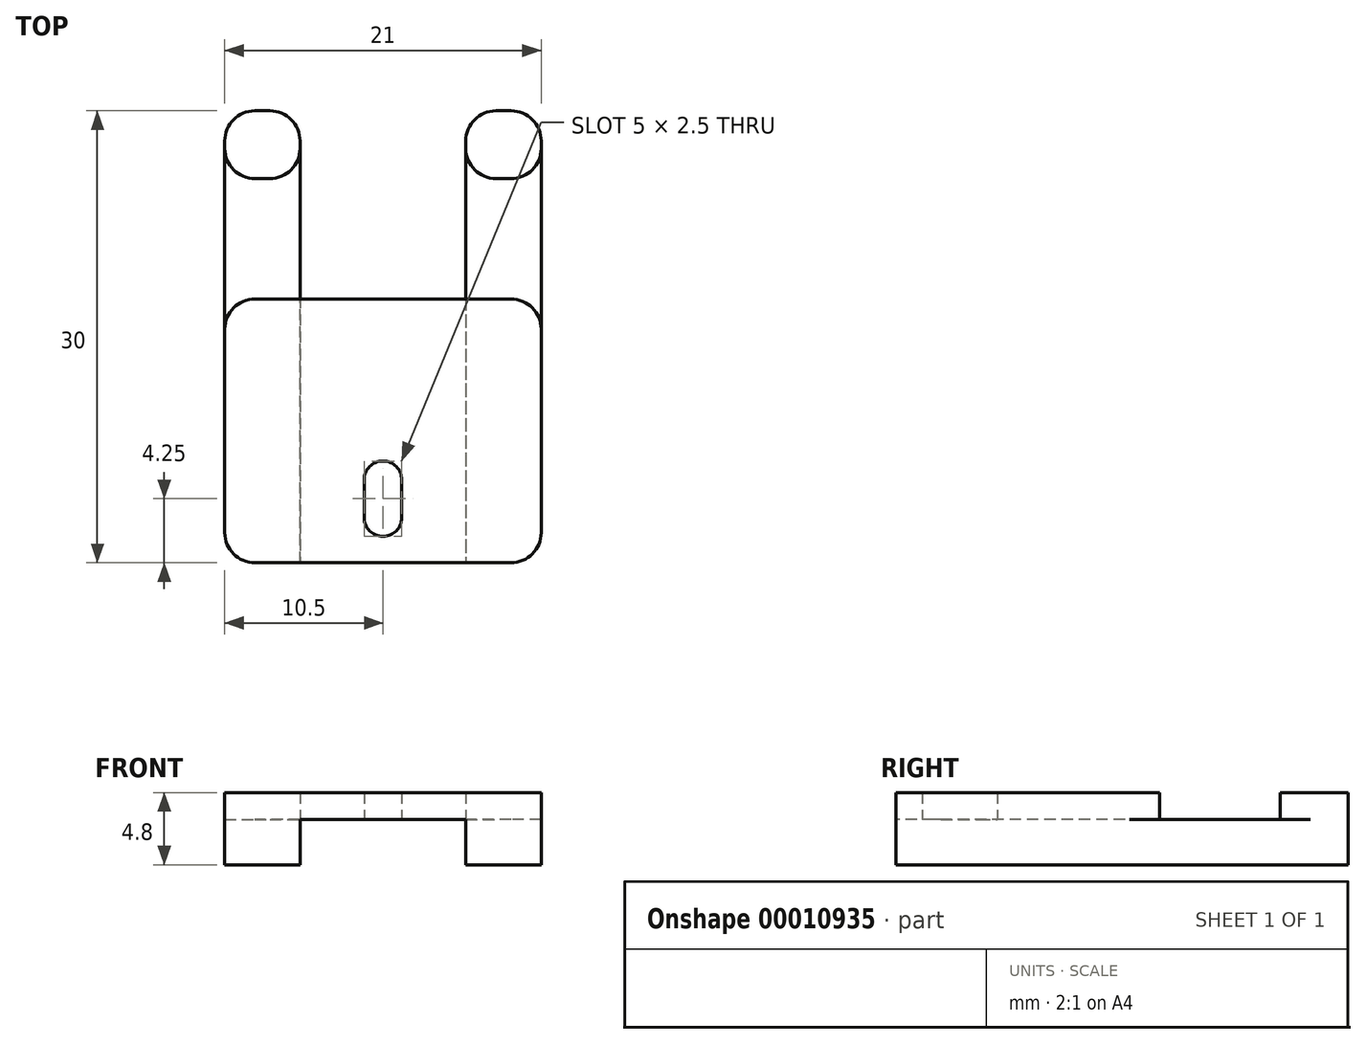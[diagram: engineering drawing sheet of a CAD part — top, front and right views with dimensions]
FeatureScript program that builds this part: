
annotation { "Feature Type Name" : "Feature", "Feature Type Description" : "" }
export const myFeature = defineFeature(function(context is Context, id is Id, definition is map)
    precondition{}
    {
        {
            var Q0;
            Q0=qCreatedBy(makeId("Top.planeOp"),FACE);
            var sketch = newSketch(context, id + "F0", { "sketchPlane" : qUnion([Q0])});
            skLineSegment(sketch, "E0", {"start": v(0, 0) * mm, "end": v(5.5, 0) * mm});
            skLineSegment(sketch, "E1.0.MirrorCS", {"start": v(0, 0) * mm, "end": v(-5.5, 0) * mm});
            skLineSegment(sketch, "E2.bottom", {"start": v(5.5, 0) * mm, "end": v(10.5, 0) * mm});
            skLineSegment(sketch, "E2.top", {"start": v(5.5, -30) * mm, "end": v(10.5, -30) * mm});
            skLineSegment(sketch, "E2.left", {"start": v(5.5, 0) * mm, "end": v(5.5, -30) * mm});
            skLineSegment(sketch, "E2.right", {"start": v(10.5, 0) * mm, "end": v(10.5, -30) * mm});
            skLineSegment(sketch, "E3.0.MirrorCS", {"start": v(-5.5, 0) * mm, "end": v(-5.5, -30) * mm});
            skLineSegment(sketch, "E4.0.MirrorCS", {"start": v(-5.5, 0) * mm, "end": v(-10.5, 0) * mm});
            skLineSegment(sketch, "E5.0.MirrorCS", {"start": v(-10.5, 0) * mm, "end": v(-10.5, -30) * mm});
            skLineSegment(sketch, "E6.0.MirrorCS", {"start": v(-5.5, -30) * mm, "end": v(-10.5, -30) * mm});
            skLineSegment(sketch, "E7", {"start": v(13, 0) * mm, "end": v(13, -4.5) * mm, "construction": true});
            skLineSegment(sketch, "E8", {"start": v(13, -4.5) * mm, "end": v(10.5, -4.5) * mm, "construction": true});
            skLineSegment(sketch, "E9", {"start": v(10.5, -4.5) * mm, "end": v(5.5, -4.5) * mm});
            skLineSegment(sketch, "E10.0.MirrorCS", {"start": v(-10.5, -4.5) * mm, "end": v(-5.5, -4.5) * mm});
            skLineSegment(sketch, "E11", {"start": v(13, -4.5) * mm, "end": v(13, -12.5) * mm, "construction": true});
            skLineSegment(sketch, "E12", {"start": v(13, -12.5) * mm, "end": v(10.5, -12.5) * mm, "construction": true});
            skLineSegment(sketch, "E13", {"start": v(10.5, -12.5) * mm, "end": v(5.5, -12.5) * mm});
            skLineSegment(sketch, "E14.0.MirrorCS", {"start": v(-10.5, -12.5) * mm, "end": v(-5.5, -12.5) * mm});
            skLineSegment(sketch, "E15", {"start": v(5.5, -12.5) * mm, "end": v(0, -12.5) * mm});
            skLineSegment(sketch, "E16", {"start": v(5.5, -30) * mm, "end": v(0, -30) * mm});
            skLineSegment(sketch, "E17.0.MirrorCS", {"start": v(-5.5, -12.5) * mm, "end": v(0, -12.5) * mm});
            skLineSegment(sketch, "E18.0.MirrorCS", {"start": v(-5.5, -30) * mm, "end": v(0, -30) * mm});
            skLineSegment(sketch, "E19", {"start": v(0, -12.5) * mm, "end": v(0, -24.5) * mm, "construction": true});
            skCircle(sketch, "E20", {"center": v(0, -24.5) * mm, "radius": 1.25 * mm});
            skLineSegment(sketch, "E21", {"start": v(-1.25, -27) * mm, "end": v(-1.25, -24.5) * mm});
            skLineSegment(sketch, "E22.0.MirrorCS", {"start": v(1.25, -27) * mm, "end": v(1.25, -24.5) * mm});
            skLineSegment(sketch, "E23", {"start": v(0, -24.5) * mm, "end": v(0, -27) * mm, "construction": true});
            skCircle(sketch, "E24", {"center": v(0, -27) * mm, "radius": 1.25 * mm});
            skSolve(sketch);
        }
        {
            var Q0;
            {var subQ2=sQuery(id+"F0.wireOp",EDGE,"E2.top");Q0=makeQuery(id+"F0.imprint","IMPRINT",FACE,{"disambiguationData":[TD([[makeQuery(id+"F0.imprint","IMPRINT",EDGE,{"derivedFrom":subQ2}),1.0]])]});}
            var Q1;
            {var subQ3=sQuery(id+"F0.wireOp",EDGE,"E15");Q1=makeQuery(id+"F0.imprint","IMPRINT",FACE,{"disambiguationData":[TD([[makeQuery(id+"F0.imprint","IMPRINT",EDGE,{"derivedFrom":subQ3}),1.0]])]});}
            var Q2;
            {var subQ1=sQuery(id+"F0.wireOp",EDGE,"E6.0.MirrorCS");Q2=makeQuery(id+"F0.imprint","IMPRINT",FACE,{"disambiguationData":[TD([[makeQuery(id+"F0.imprint","IMPRINT",EDGE,{"derivedFrom":subQ1}),-1.0]])]});}
            var Q3;
            {var subQ2=sQuery(id+"F0.wireOp",EDGE,"E2.bottom");Q3=makeQuery(id+"F0.imprint","IMPRINT",FACE,{"disambiguationData":[TD([[makeQuery(id+"F0.imprint","IMPRINT",EDGE,{"derivedFrom":subQ2}),-1.0]])]});}
            var Q4;
            {var subQ2=sQuery(id+"F0.wireOp",EDGE,"E4.0.MirrorCS");Q4=makeQuery(id+"F0.imprint","IMPRINT",FACE,{"disambiguationData":[TD([[makeQuery(id+"F0.imprint","IMPRINT",EDGE,{"derivedFrom":subQ2}),1.0]])]});}
            extrude(context, id + "F1", {"entities" : qUnion([Q0, Q1, Q2, Q3, Q4]), "depth" : 1.8 * mm});
        }
        {
            var Q0;
            {var subQ2=sQuery(id+"F0.wireOp",EDGE,"E4.0.MirrorCS");Q0=makeQuery(id+"F0.imprint","IMPRINT",FACE,{"disambiguationData":[TD([[makeQuery(id+"F0.imprint","IMPRINT",EDGE,{"derivedFrom":subQ2}),1.0]])]});}
            var Q1;
            {var subQ1=sQuery(id+"F0.wireOp",EDGE,"E10.0.MirrorCS");Q1=makeQuery(id+"F0.imprint","IMPRINT",FACE,{"disambiguationData":[TD([[makeQuery(id+"F0.imprint","IMPRINT",EDGE,{"derivedFrom":subQ1}),-1.0]])]});}
            var Q2;
            {var subQ1=sQuery(id+"F0.wireOp",EDGE,"E6.0.MirrorCS");Q2=makeQuery(id+"F0.imprint","IMPRINT",FACE,{"disambiguationData":[TD([[makeQuery(id+"F0.imprint","IMPRINT",EDGE,{"derivedFrom":subQ1}),-1.0]])]});}
            var Q3;
            {var subQ2=sQuery(id+"F0.wireOp",EDGE,"E2.top");Q3=makeQuery(id+"F0.imprint","IMPRINT",FACE,{"disambiguationData":[TD([[makeQuery(id+"F0.imprint","IMPRINT",EDGE,{"derivedFrom":subQ2}),1.0]])]});}
            var Q4;
            {var subQ1=sQuery(id+"F0.wireOp",EDGE,"E9");Q4=makeQuery(id+"F0.imprint","IMPRINT",FACE,{"disambiguationData":[TD([[makeQuery(id+"F0.imprint","IMPRINT",EDGE,{"derivedFrom":subQ1}),1.0]])]});}
            var Q5;
            {var subQ2=sQuery(id+"F0.wireOp",EDGE,"E2.bottom");Q5=makeQuery(id+"F0.imprint","IMPRINT",FACE,{"disambiguationData":[TD([[makeQuery(id+"F0.imprint","IMPRINT",EDGE,{"derivedFrom":subQ2}),-1.0]])]});}
            extrude(context, id + "F2", {"entities" : qUnion([Q0, Q1, Q2, Q3, Q4, Q5]), "oppositeDirection" : true, "depth" : 3 * mm});
        }
        {
            var Q0;
            Q0=makeQuery(id+"F2.opExtrude","SWEPT_BODY",BODY,{"disambiguationData":[OSD([sQuery(id+"F0.wireOp",EDGE,"E2.bottom"),sQuery(id+"F0.wireOp",EDGE,"E2.top"),sQuery(id+"F0.wireOp",EDGE,"E2.left"),sQuery(id+"F0.wireOp",EDGE,"E2.right")])]});
            var Q1;
            Q1=makeQuery(id+"F1.opExtrude","SWEPT_BODY",BODY,{"disambiguationData":[OSD([sQuery(id+"F0.wireOp",EDGE,"E2.bottom"),sQuery(id+"F0.wireOp",EDGE,"E2.left"),sQuery(id+"F0.wireOp",EDGE,"E2.right"),sQuery(id+"F0.wireOp",EDGE,"E9")])]});
            var Q2;
            Q2=makeQuery(id+"F1.opExtrude","SWEPT_BODY",BODY,{"disambiguationData":[OSD([sQuery(id+"F0.wireOp",EDGE,"E2.top"),sQuery(id+"F0.wireOp",EDGE,"E2.right"),sQuery(id+"F0.wireOp",EDGE,"E5.0.MirrorCS"),sQuery(id+"F0.wireOp",EDGE,"E6.0.MirrorCS"),sQuery(id+"F0.wireOp",EDGE,"E13"),sQuery(id+"F0.wireOp",EDGE,"E14.0.MirrorCS"),sQuery(id+"F0.wireOp",EDGE,"E15"),sQuery(id+"F0.wireOp",EDGE,"E16"),sQuery(id+"F0.wireOp",EDGE,"E17.0.MirrorCS"),sQuery(id+"F0.wireOp",EDGE,"E18.0.MirrorCS"),sQuery(id+"F0.wireOp",EDGE,"E20")])]});
            var Q3;
            Q3=makeQuery(id+"F1.opExtrude","SWEPT_BODY",BODY,{"disambiguationData":[OSD([sQuery(id+"F0.wireOp",EDGE,"E3.0.MirrorCS"),sQuery(id+"F0.wireOp",EDGE,"E4.0.MirrorCS"),sQuery(id+"F0.wireOp",EDGE,"E5.0.MirrorCS"),sQuery(id+"F0.wireOp",EDGE,"E10.0.MirrorCS")])]});
            var Q4;
            Q4=makeQuery(id+"F2.opExtrude","SWEPT_BODY",BODY,{"disambiguationData":[OSD([sQuery(id+"F0.wireOp",EDGE,"E3.0.MirrorCS"),sQuery(id+"F0.wireOp",EDGE,"E4.0.MirrorCS"),sQuery(id+"F0.wireOp",EDGE,"E5.0.MirrorCS"),sQuery(id+"F0.wireOp",EDGE,"E6.0.MirrorCS")])]});
            booleanBodies(context, id + "F3", {"operationType" : BooleanOperationType.UNION, "tools" : qUnion([Q0, Q1, Q2, Q3, Q4])});
        }
        {
            var Q0;
            {var subQ0=sQuery(id+"F0.wireOp",EDGE,"E2.bottom");var subQ1=sQuery(id+"F0.wireOp",EDGE,"E2.right");Q0=makeQuery(id+"F3.opBoolean","MERGE",EDGE,{"derivedFrom":[makeQuery(id+"F1.opExtrude","SWEPT_EDGE",EDGE,{"disambiguationData":[OSD([subQ0,subQ1])]}),makeQuery(id+"F2.opExtrude","SWEPT_EDGE",EDGE,{"disambiguationData":[OSD([subQ0,subQ1])]})]});}
            var Q1;
            {var subQ0=sQuery(id+"F0.wireOp",EDGE,"E0");var subQ1=sQuery(id+"F0.wireOp",EDGE,"E2.bottom");var subQ2=sQuery(id+"F0.wireOp",EDGE,"E2.left");Q1=makeQuery(id+"F3.opBoolean","MERGE",EDGE,{"derivedFrom":[makeQuery(id+"F1.opExtrude","SWEPT_EDGE",EDGE,{"disambiguationData":[OSD([subQ0,subQ1,subQ2])]}),makeQuery(id+"F2.opExtrude","SWEPT_EDGE",EDGE,{"disambiguationData":[OSD([subQ0,subQ1,subQ2])]})]});}
            var Q2;
            {var subQ0=sQuery(id+"F0.wireOp",EDGE,"E1.0.MirrorCS");var subQ1=sQuery(id+"F0.wireOp",EDGE,"E3.0.MirrorCS");var subQ2=sQuery(id+"F0.wireOp",EDGE,"E4.0.MirrorCS");Q2=makeQuery(id+"F3.opBoolean","MERGE",EDGE,{"derivedFrom":[makeQuery(id+"F1.opExtrude","SWEPT_EDGE",EDGE,{"disambiguationData":[OSD([subQ0,subQ1,subQ2])]}),makeQuery(id+"F2.opExtrude","SWEPT_EDGE",EDGE,{"disambiguationData":[OSD([subQ0,subQ1,subQ2])]})]});}
            var Q3;
            {var subQ0=sQuery(id+"F0.wireOp",EDGE,"E4.0.MirrorCS");var subQ1=sQuery(id+"F0.wireOp",EDGE,"E5.0.MirrorCS");Q3=makeQuery(id+"F3.opBoolean","MERGE",EDGE,{"derivedFrom":[makeQuery(id+"F1.opExtrude","SWEPT_EDGE",EDGE,{"disambiguationData":[OSD([subQ0,subQ1])]}),makeQuery(id+"F2.opExtrude","SWEPT_EDGE",EDGE,{"disambiguationData":[OSD([subQ0,subQ1])]})]});}
            var Q4;
            Q4=makeQuery(id+"F1.opExtrude","SWEPT_EDGE",EDGE,{"disambiguationData":[OSD([sQuery(id+"F0.wireOp",EDGE,"E2.right"),sQuery(id+"F0.wireOp",EDGE,"E8"),sQuery(id+"F0.wireOp",EDGE,"E9")])]});
            var Q5;
            Q5=makeQuery(id+"F1.opExtrude","SWEPT_EDGE",EDGE,{"disambiguationData":[OSD([sQuery(id+"F0.wireOp",EDGE,"E3.0.MirrorCS"),sQuery(id+"F0.wireOp",EDGE,"E10.0.MirrorCS")])]});
            var Q6;
            Q6=makeQuery(id+"F1.opExtrude","SWEPT_EDGE",EDGE,{"disambiguationData":[OSD([sQuery(id+"F0.wireOp",EDGE,"E2.left"),sQuery(id+"F0.wireOp",EDGE,"E9")])]});
            var Q7;
            Q7=makeQuery(id+"F1.opExtrude","SWEPT_EDGE",EDGE,{"disambiguationData":[OSD([sQuery(id+"F0.wireOp",EDGE,"E5.0.MirrorCS"),sQuery(id+"F0.wireOp",EDGE,"E10.0.MirrorCS")])]});
            var Q8;
            Q8=makeQuery(id+"F1.opExtrude","SWEPT_EDGE",EDGE,{"disambiguationData":[OSD([sQuery(id+"F0.wireOp",EDGE,"E2.right"),sQuery(id+"F0.wireOp",EDGE,"E12"),sQuery(id+"F0.wireOp",EDGE,"E13")])]});
            var Q9;
            Q9=makeQuery(id+"F1.opExtrude","SWEPT_EDGE",EDGE,{"disambiguationData":[OSD([sQuery(id+"F0.wireOp",EDGE,"E5.0.MirrorCS"),sQuery(id+"F0.wireOp",EDGE,"E14.0.MirrorCS")])]});
            var Q10;
            {var subQ0=sQuery(id+"F0.wireOp",EDGE,"E2.top");var subQ1=sQuery(id+"F0.wireOp",EDGE,"E2.right");Q10=makeQuery(id+"F3.opBoolean","MERGE",EDGE,{"derivedFrom":[makeQuery(id+"F1.opExtrude","SWEPT_EDGE",EDGE,{"disambiguationData":[OSD([subQ0,subQ1])]}),makeQuery(id+"F2.opExtrude","SWEPT_EDGE",EDGE,{"disambiguationData":[OSD([subQ0,subQ1])]})]});}
            var Q11;
            {var subQ0=sQuery(id+"F0.wireOp",EDGE,"E5.0.MirrorCS");var subQ1=sQuery(id+"F0.wireOp",EDGE,"E6.0.MirrorCS");Q11=makeQuery(id+"F3.opBoolean","MERGE",EDGE,{"derivedFrom":[makeQuery(id+"F1.opExtrude","SWEPT_EDGE",EDGE,{"disambiguationData":[OSD([subQ0,subQ1])]}),makeQuery(id+"F2.opExtrude","SWEPT_EDGE",EDGE,{"disambiguationData":[OSD([subQ0,subQ1])]})]});}
            fillet(context, id + "F4", {"entities" : qUnion([Q0, Q1, Q2, Q3, Q4, Q5, Q6, Q7, Q8, Q9, Q10, Q11]), "radius" : 2 * mm, "tangentPropagation" : true, "allowEdgeOverflow" : false});
        }
    });
